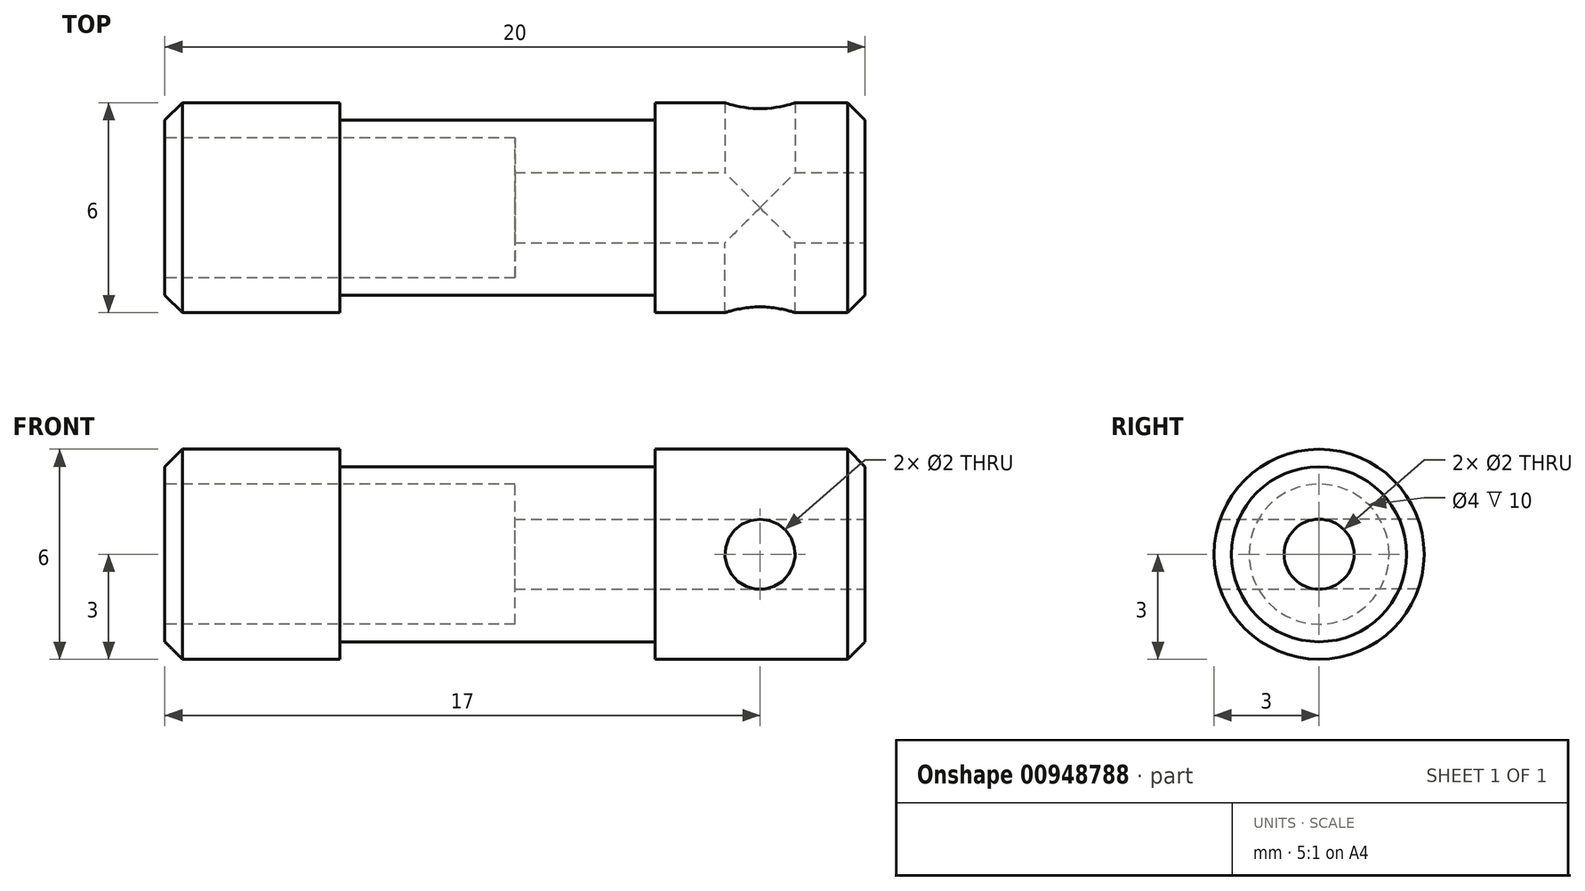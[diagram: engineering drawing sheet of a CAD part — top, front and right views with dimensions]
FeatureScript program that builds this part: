
annotation { "Feature Type Name" : "Feature", "Feature Type Description" : "" }
export const myFeature = defineFeature(function(context is Context, id is Id, definition is map)
    precondition{}
    {
        {
            var Q0;
            Q0=qCreatedBy(makeId("Right.planeOp"),FACE);
            var sketch = newSketch(context, id + "F0", { "sketchPlane" : qUnion([Q0])});
            skCircle(sketch, "E0", {"center": v(0, 0) * mm, "radius": 2 * mm});
            skCircle(sketch, "E1", {"center": v(0, 0) * mm, "radius": 3 * mm});
            skCircle(sketch, "E2", {"center": v(0, 0) * mm, "radius": 2.5 * mm});
            skSolve(sketch);
        }
        {
            var Q0;
            Q0=makeQuery(id+"F0.imprint","IMPRINT",FACE,{"disambiguationData":[TD([[makeQuery(id+"F0.imprint","IMPRINT",EDGE,{"derivedFrom":sQuery(id+"F0.wireOp",EDGE,"E0")}),-1.0]])]});
            var Q1;
            Q1=makeQuery(id+"F0.imprint","IMPRINT",FACE,{"disambiguationData":[TD([[makeQuery(id+"F0.imprint","IMPRINT",EDGE,{"derivedFrom":sQuery(id+"F0.wireOp",EDGE,"E0")}),1.0]])]});
            extrude(context, id + "F1", {"entities" : qUnion([Q0, Q1]), "depth" : 20 * mm, "offsetDistance" : 25 * mm});
        }
        {
            var Q0;
            Q0=makeQuery(id+"F0.imprint","IMPRINT",FACE,{"disambiguationData":[TD([[makeQuery(id+"F0.imprint","IMPRINT",EDGE,{"derivedFrom":sQuery(id+"F0.wireOp",EDGE,"E1")}),1.0]])]});
            extrude(context, id + "F2", {"entities" : qUnion([Q0]), "operationType" : NewBodyOperationType.ADD, "depth" : 5 * mm, "offsetDistance" : 25 * mm});
        }
        {
            var Q0;
            Q0=makeQuery(id+"F0.imprint","IMPRINT",FACE,{"disambiguationData":[TD([[makeQuery(id+"F0.imprint","IMPRINT",EDGE,{"derivedFrom":sQuery(id+"F0.wireOp",EDGE,"E0")}),1.0]])]});
            extrude(context, id + "F3", {"entities" : qUnion([Q0]), "operationType" : NewBodyOperationType.REMOVE, "depth" : 10 * mm, "offsetDistance" : 25 * mm});
        }
        {
            var Q0;
            Q0=makeQuery(id+"F1.opExtrude","CAP_FACE",FACE,{"disambiguationData":[OSD([sQuery(id+"F0.wireOp",EDGE,"E2")])],"isStart":false});
            var sketch = newSketch(context, id + "F4", { "sketchPlane" : qUnion([Q0])});
            skCircle(sketch, "E3", {"center": v(0, 0) * mm, "radius": 1 * mm});
            skCircle(sketch, "E4", {"center": v(0, 0) * mm, "radius": 3 * mm});
            skSolve(sketch);
        }
        {
            var Q0;
            Q0=makeQuery(id+"F4.imprint","IMPRINT",FACE,{"disambiguationData":[TD([[makeQuery(id+"F4.imprint","IMPRINT",EDGE,{"derivedFrom":sQuery(id+"F4.wireOp",EDGE,"E4")}),1.0]])]});
            extrude(context, id + "F5", {"entities" : qUnion([Q0]), "operationType" : NewBodyOperationType.ADD, "oppositeDirection" : true, "depth" : 6 * mm, "offsetDistance" : 25 * mm});
        }
        {
            var Q0;
            Q0=makeQuery(id+"F4.imprint","IMPRINT",FACE,{"disambiguationData":[TD([[makeQuery(id+"F4.imprint","IMPRINT",EDGE,{"derivedFrom":sQuery(id+"F4.wireOp",EDGE,"E3")}),1.0]])]});
            extrude(context, id + "F6", {"entities" : qUnion([Q0]), "operationType" : NewBodyOperationType.REMOVE, "oppositeDirection" : true, "depth" : 10 * mm, "offsetDistance" : 25 * mm});
        }
        {
            var Q0;
            Q0=makeQuery(id+"F5.opExtrude","CAP_EDGE",EDGE,{"disambiguationData":[OSD([sQuery(id+"F4.wireOp",EDGE,"E4")])],"isStart":true});
            var Q1;
            Q1=makeQuery(id+"F2.opExtrude","CAP_EDGE",EDGE,{"disambiguationData":[OSD([sQuery(id+"F0.wireOp",EDGE,"E1")])],"isStart":true});
            chamfer(context, id + "F7", {"entities" : qUnion([Q0, Q1]), "width" : 0.5 * mm, "tangentPropagation" : true});
        }
        {
            var Q0;
            Q0=qCreatedBy(makeId("Front.planeOp"),FACE);
            var sketch = newSketch(context, id + "F8", { "sketchPlane" : qUnion([Q0])});
            skLineSegment(sketch, "E5", {"start": v(0, 0) * mm, "end": v(20, 0) * mm});
            skCircle(sketch, "E6", {"center": v(3, 0) * mm, "radius": 1 * mm});
            skCircle(sketch, "E7", {"center": v(17, 0) * mm, "radius": 1 * mm});
            skSolve(sketch);
        }
        {
            var Q0;
            {var subQ0=sQuery(id+"F8.wireOp",EDGE,"E6");var subQ1=sQuery(id+"F8.wireOp",EDGE,"E5");var subQ2=makeQuery(id+"F8.imprint","INTERSECT",VERTEX,{"disambiguationData":[OD(0.0)],"derivedFrom":[subQ1,subQ0]});Q0=makeQuery(id+"F8.imprint","IMPRINT",FACE,{"disambiguationData":[TD([[makeQuery(id+"F8.imprint","IMPRINT",EDGE,{"disambiguationData":[TD([[subQ2,-1.0]])],"derivedFrom":subQ1}),1.0]])]});}
            var Q1;
            {var subQ0=sQuery(id+"F8.wireOp",EDGE,"E6");var subQ1=sQuery(id+"F8.wireOp",EDGE,"E5");var subQ2=makeQuery(id+"F8.imprint","INTERSECT",VERTEX,{"disambiguationData":[OD(0.0)],"derivedFrom":[subQ1,subQ0]});Q1=makeQuery(id+"F8.imprint","IMPRINT",FACE,{"disambiguationData":[TD([[makeQuery(id+"F8.imprint","IMPRINT",EDGE,{"disambiguationData":[TD([[subQ2,-1.0]])],"derivedFrom":subQ1}),-1.0]])]});}
            var Q2;
            {var subQ0=sQuery(id+"F8.wireOp",EDGE,"E7");var subQ1=sQuery(id+"F8.wireOp",EDGE,"E5");var subQ2=makeQuery(id+"F8.imprint","INTERSECT",VERTEX,{"disambiguationData":[OD(0.0)],"derivedFrom":[subQ1,subQ0]});Q2=makeQuery(id+"F8.imprint","IMPRINT",FACE,{"disambiguationData":[TD([[makeQuery(id+"F8.imprint","IMPRINT",EDGE,{"disambiguationData":[TD([[subQ2,-1.0]])],"derivedFrom":subQ1}),-1.0]])]});}
            var Q3;
            {var subQ0=sQuery(id+"F8.wireOp",EDGE,"E7");var subQ1=sQuery(id+"F8.wireOp",EDGE,"E5");var subQ2=makeQuery(id+"F8.imprint","INTERSECT",VERTEX,{"disambiguationData":[OD(0.0)],"derivedFrom":[subQ1,subQ0]});Q3=makeQuery(id+"F8.imprint","IMPRINT",FACE,{"disambiguationData":[TD([[makeQuery(id+"F8.imprint","IMPRINT",EDGE,{"disambiguationData":[TD([[subQ2,-1.0]])],"derivedFrom":subQ1}),1.0]])]});}
            extrude(context, id + "F9", {"entities" : qUnion([Q0, Q1, Q2, Q3]), "operationType" : NewBodyOperationType.REMOVE, "oppositeDirection" : true, "depth" : 25 * mm, "offsetDistance" : 25 * mm});
        }
        {
            var Q0;
            {var subQ0=sQuery(id+"F8.wireOp",EDGE,"E7");var subQ1=sQuery(id+"F8.wireOp",EDGE,"E5");var subQ2=makeQuery(id+"F8.imprint","INTERSECT",VERTEX,{"disambiguationData":[OD(0.0)],"derivedFrom":[subQ1,subQ0]});Q0=makeQuery(id+"F8.imprint","IMPRINT",FACE,{"disambiguationData":[TD([[makeQuery(id+"F8.imprint","IMPRINT",EDGE,{"disambiguationData":[TD([[subQ2,-1.0]])],"derivedFrom":subQ1}),1.0]])]});}
            var Q1;
            {var subQ0=sQuery(id+"F8.wireOp",EDGE,"E7");var subQ1=sQuery(id+"F8.wireOp",EDGE,"E5");var subQ2=makeQuery(id+"F8.imprint","INTERSECT",VERTEX,{"disambiguationData":[OD(0.0)],"derivedFrom":[subQ1,subQ0]});Q1=makeQuery(id+"F8.imprint","IMPRINT",FACE,{"disambiguationData":[TD([[makeQuery(id+"F8.imprint","IMPRINT",EDGE,{"disambiguationData":[TD([[subQ2,-1.0]])],"derivedFrom":subQ1}),-1.0]])]});}
            var Q2;
            {var subQ0=sQuery(id+"F8.wireOp",EDGE,"E6");var subQ1=sQuery(id+"F8.wireOp",EDGE,"E5");var subQ2=makeQuery(id+"F8.imprint","INTERSECT",VERTEX,{"disambiguationData":[OD(0.0)],"derivedFrom":[subQ1,subQ0]});Q2=makeQuery(id+"F8.imprint","IMPRINT",FACE,{"disambiguationData":[TD([[makeQuery(id+"F8.imprint","IMPRINT",EDGE,{"disambiguationData":[TD([[subQ2,-1.0]])],"derivedFrom":subQ1}),1.0]])]});}
            var Q3;
            {var subQ0=sQuery(id+"F8.wireOp",EDGE,"E6");var subQ1=sQuery(id+"F8.wireOp",EDGE,"E5");var subQ2=makeQuery(id+"F8.imprint","INTERSECT",VERTEX,{"disambiguationData":[OD(0.0)],"derivedFrom":[subQ1,subQ0]});Q3=makeQuery(id+"F8.imprint","IMPRINT",FACE,{"disambiguationData":[TD([[makeQuery(id+"F8.imprint","IMPRINT",EDGE,{"disambiguationData":[TD([[subQ2,-1.0]])],"derivedFrom":subQ1}),-1.0]])]});}
            extrude(context, id + "F10", {"entities" : qUnion([Q0, Q1, Q2, Q3]), "operationType" : NewBodyOperationType.REMOVE, "depth" : 25 * mm, "offsetDistance" : 25 * mm});
        }
    });
